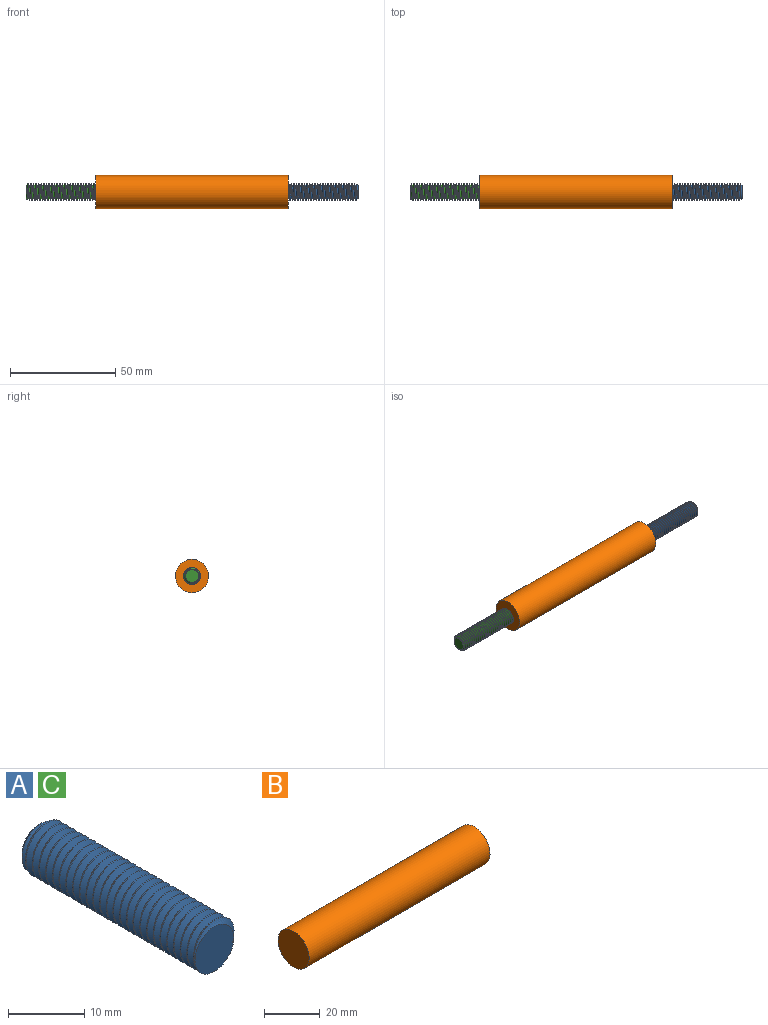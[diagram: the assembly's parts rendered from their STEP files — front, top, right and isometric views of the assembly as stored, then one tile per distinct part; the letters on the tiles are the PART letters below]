
ASSEMBLY  parts=3 mates=2
PART A: 8 faces, bbox 8.5x34.6x8.5 mm
  f0: cylinder r=4mm len=32.08mm, axis (0,1,0), area 100.8mm2, adj f2,f4,f6,f7
  f1: cone r=3.06mm half-angle=45deg, axis (0,-1,0), area 12.7mm2, adj f2,f3,f4,f5
  f2: cone r=3.06mm half-angle=45deg, axis (0,-1,0), area 3.4mm2, adj f0,f1,f4,f6
  f3: plane 6.13x6.13mm, normal (0,1,0), area 29.5mm2, adj f1
  f4: bspline ~34.06x8mm, area 550.6mm2, adj f0,f1,f2,f5,f7
  f5: cylinder r=3.19mm len=32.89mm, axis (0,1,0), area 82.2mm2, adj f1,f4,f6,f7
  f6: bspline ~33.59x8mm, area 550mm2, adj f0,f2,f5,f7
  f7: plane 7.73x7.73mm, normal (0,-1,0), area 40.8mm2, adj f0,f4,f5,f6
PART B: 3 faces, bbox 91.4x15.7x15.7 mm
  f0: plane 15.75x15.75mm, normal (-1,0,0), area 194.8mm2, adj f1
  f1: cylinder r=7.87mm len=91.44mm, axis (-1,0,0), area 4523.9mm2, adj f0,f2
  f2: plane 15.75x15.75mm, normal (1,0,0), area 194.8mm2, adj f1
PART C: same geometry as A
PLACE A rot(axis=(0.58,0.58,-0.58),120deg) t=(42.36,1.95,0.3)mm
PLACE B t=(3.02,1.95,0.3)mm
PLACE C rot(axis=(0.58,-0.58,0.58),120deg) t=(-36.32,1.95,0.3)mm
MATE planar C.f5 <-> B.f1  axis (1,0,0) through (-42.7,1.95,0.3)mm
MATE planar A.f5 <-> B.f1  axis (-1,0,0) through (48.74,1.95,0.3)mm
